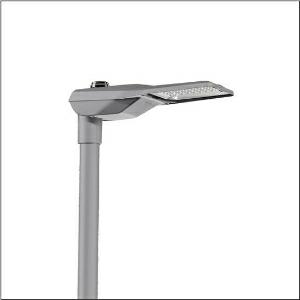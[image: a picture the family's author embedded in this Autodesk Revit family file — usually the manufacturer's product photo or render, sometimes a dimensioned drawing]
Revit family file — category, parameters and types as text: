
# Revit family: streetlight_sl_21_mini___stw1_0a_5xe6e47n08gb_debc
name_source: partatom
category: Lighting Fixtures
units: mm (PartAtom-declared; Revit-internal decimal feet)

## family parameters
Cut with Voids When Loaded = No
Host = Face
Light Source = No
Part Type = Normal
Room Calculation Point = No
Round Connector Dimension = Use Diameter
Shared = No

## types (1)
- --- (1 x LED, 6180 lm, 40.4 W, 4000K)
    Apparent Load = 40 VA
    CIE Flux Codes = 38 75 98 100 100
    Color Rendering = 70
    Color Temperature = 4000K
    Default Elevation = 1800 mm
    Description = Streetlight SL 21 mini, mast luminaire, primary light control with lens, of PMMA, primary optical cover: cover, of toughened safety glass, transparent, light distribution: STW1.0a, light emission: direct distribution, primary light characteristic: asymmetric, installation type: side-entry, LED, 3G 1.5mm², High Power LED, rated luminous flux: 6.180lm, luminous efficacy: 153lm/W, light colour: 740, colour temperature: 4000K, control gear: NEMA (7pin), control: overheat protection, pre-setting: linear dimming characteristic, constant luminous flux control, time-dependent luminous flux control, flexible luminous flux parameterisation, mains connection: 230..240V, AC, 50/60Hz, connection cable pre-assembled, cable length: 8,5m, wiring characteristics: H07RN-F, start of lifetime: 40W, end of service life: 41W, reduction: 19W, luminaire housing, of diecast aluminium (EN AC-44300), powder-coated, SITECO metallic grey (DB 702S), corrosivity category C5 high according to DIN EN ISO 12944, multi-level sealing system, sealing non-destructively replaceable, inclination adjustable: 0°, 5°, 10°, 15°, length: 628mm, width: 235mm, height: 110mm, spigot size: 42mm (side-entry), mounting height: 4..8m, protection rating (complete): IP66, insulation class (complete): insulation class I (protective earthing), certification: CE, ENEC, ENEC+, VDE, impact resistance: IK10, permissible operating ambient temperature for outdoor applications: -40..+50°C, standard-compliant lighting for roads and squares, packaging unit: 1 piece

Light Distribution: STW1.0a
    Height = 110 mm
    Lamp = 1 x LED
    Lamp Light Flux = 6180 lm
    Lamp Power = 40.4 W
    Lamp count = 1
    Length = 625 mm
    Luminous efficacy = 153 lm/W
    Manufacturer = Siteco
    ModVariant = No
    Model = 5XE6E47N08GB
    Number of Poles = 1
    OnlyDefault = Yes
    Power Factor = 1
    Product Name = Streetlight SL 21 mini | STW1.0a
    Product group = mast luminaire | pylon top
    ProductGroupID = 6100
    Protection Class = Protection class I
    Protection Degree = IP 66
    RLX_Detail_Level = 1
    RLX_Emergency_Light_Flux = 0 lm
    RLX_Emergency_Type = 0
    RLX_Emergency_Type_DB = No
    RlxData = <blob elided: 25869 chars, md5=916f8647>
    Socket = socket
    Standby Power = 0 W
    System Light Flux = 6180 lm
    System Power = 40 W
    Type Comments = factory setting: luminous flux: 100 % | dim-lin: 254 | 812 mA
    Type Image = l_1294379.jpg
    URL = http://relux.com
    VarID = @adj_135133
    Voltage = 0 V
    Weight = 0.00 kg
    Width = 234 mm

## geometry (parser evidence)
native form markers: Blend x4, Sweep x11
no freeform markers — native parametric forms only
